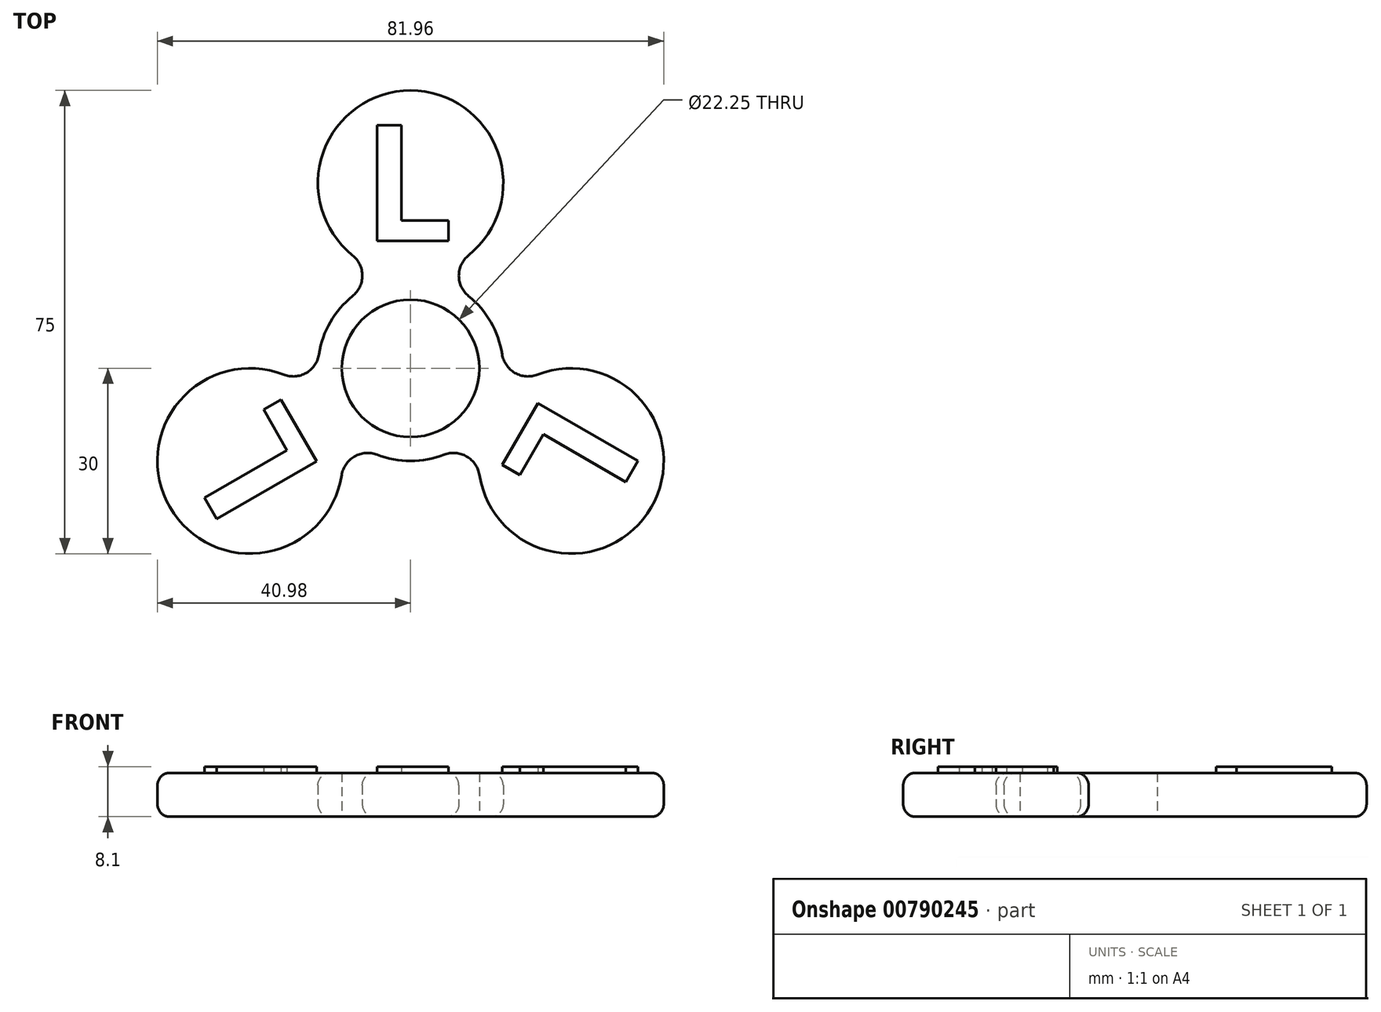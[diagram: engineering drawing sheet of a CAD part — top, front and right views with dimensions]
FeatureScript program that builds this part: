
annotation { "Feature Type Name" : "Feature", "Feature Type Description" : "" }
export const myFeature = defineFeature(function(context is Context, id is Id, definition is map)
    precondition{}
    {
        {
            var Q0;
            Q0=qCreatedBy(makeId("Top.planeOp"),FACE);
            var sketch = newSketch(context, id + "F0", { "sketchPlane" : qUnion([Q0])});
            skCircle(sketch, "E0", {"center": v(0, 0) * mm, "radius": 15 * mm});
            skCircle(sketch, "E1", {"center": v(0, 0) * mm, "radius": 11.12 * mm});
            skSolve(sketch);
        }
        {
            var Q0;
            Q0 = qSketchRegion(id + "F0", true);
            extrude(context, id + "F1", {"entities" : qUnion([Q0]), "depth" : 7.1 * mm, "offsetDistance" : 25 * mm});
        }
        {
            var Q0;
            Q0=qCreatedBy(makeId("Top.planeOp"),FACE);
            var sketch = newSketch(context, id + "F2", { "sketchPlane" : qUnion([Q0])});
            skArc(sketch, "E2", {"start": v(-9.4, 11.69) * mm, "mid": v(-7.81, 15) * mm, "end": v(-9.4, 18.31) * mm});
            skArc(sketch, "E3.MirrorCS", {"start": v(9.4, 11.69) * mm, "mid": v(7.81, 15) * mm, "end": v(9.4, 18.31) * mm});
            skArc(sketch, "E4", {"start": v(9.4, 18.31) * mm, "mid": v(0, 45) * mm, "end": v(-9.4, 18.31) * mm});
            skArc(sketch, "E5", {"start": v(9.4, 11.69) * mm, "mid": v(0, 15) * mm, "end": v(-9.4, 11.69) * mm});
            skArc(sketch, "E6.1.0", {"start": v(-5.42, -13.99) * mm, "mid": v(-9.08, -14.27) * mm, "end": v(-11.16, -17.3) * mm});
            skArc(sketch, "E6.1.1", {"start": v(-14.82, 2.3) * mm, "mid": v(-13, -7.5) * mm, "end": v(-5.42, -13.99) * mm});
            skArc(sketch, "E6.1.2", {"start": v(-14.82, 2.3) * mm, "mid": v(-16.9, -0.73) * mm, "end": v(-20.56, -1.01) * mm});
            skArc(sketch, "E6.1.3", {"start": v(-20.56, -1.01) * mm, "mid": v(-38.97, -22.5) * mm, "end": v(-11.16, -17.3) * mm});
            skArc(sketch, "E6.2.0", {"start": v(14.82, 2.3) * mm, "mid": v(16.9, -0.73) * mm, "end": v(20.56, -1.01) * mm});
            skArc(sketch, "E6.2.1", {"start": v(5.42, -13.99) * mm, "mid": v(13, -7.5) * mm, "end": v(14.82, 2.3) * mm});
            skArc(sketch, "E6.2.2", {"start": v(5.42, -13.99) * mm, "mid": v(9.08, -14.27) * mm, "end": v(11.16, -17.3) * mm});
            skArc(sketch, "E6.2.3", {"start": v(11.16, -17.3) * mm, "mid": v(38.97, -22.5) * mm, "end": v(20.56, -1.01) * mm});
            skSolve(sketch);
        }
        {
            var Q0;
            Q0 = qSketchRegion(id + "F2", true);
            extrude(context, id + "F3", {"entities" : qUnion([Q0]), "operationType" : NewBodyOperationType.ADD, "depth" : 7.1 * mm, "offsetDistance" : 25 * mm});
        }
        {
            var Q0;
            Q0=makeQuery(id+"F3.boolean.opBoolean","MERGE",FACE,{"derivedFrom":[makeQuery(id+"F1.opExtrude","CAP_FACE",FACE,{"disambiguationData":[OSD([sQuery(id+"F0.wireOp",EDGE,"E0"),sQuery(id+"F0.wireOp",EDGE,"E1")])],"isStart":false}),makeQuery(id+"F3.opExtrude","CAP_FACE",FACE,{"disambiguationData":[OSD([sQuery(id+"F2.wireOp",EDGE,"E2"),sQuery(id+"F2.wireOp",EDGE,"E3.MirrorCS"),sQuery(id+"F2.wireOp",EDGE,"E4"),sQuery(id+"F2.wireOp",EDGE,"E5")])],"isStart":false}),makeQuery(id+"F3.opExtrude","CAP_FACE",FACE,{"disambiguationData":[OSD([sQuery(id+"F2.wireOp",EDGE,"E6.1.0"),sQuery(id+"F2.wireOp",EDGE,"E6.1.1"),sQuery(id+"F2.wireOp",EDGE,"E6.1.2"),sQuery(id+"F2.wireOp",EDGE,"E6.1.3")])],"isStart":false}),makeQuery(id+"F3.opExtrude","CAP_FACE",FACE,{"disambiguationData":[OSD([sQuery(id+"F2.wireOp",EDGE,"E6.2.0"),sQuery(id+"F2.wireOp",EDGE,"E6.2.1"),sQuery(id+"F2.wireOp",EDGE,"E6.2.2"),sQuery(id+"F2.wireOp",EDGE,"E6.2.3")])],"isStart":false})]});
            var sketch = newSketch(context, id + "F4", { "sketchPlane" : qUnion([Q0])});
            skText(sketch, "E7", { "text": "L", "fontName": "OpenSans-Bold.ttf"});
            const initialGuessF4  = {"E7": [-0.0078, 0.02067, 1, 0, 0.01886]};
            skSetInitialGuess(sketch, initialGuessF4);
            skSolve(sketch);
        }
        {
            var Q0;
            Q0 = qSketchRegion(id + "F4", true);
            extrude(context, id + "F5", {"entities" : qUnion([Q0]), "depth" : 1 * mm, "offsetDistance" : 25 * mm});
        }
        {
            var Q0;
            Q0=qCreatedBy(makeId("Front.planeOp"),FACE);
            var sketch = newSketch(context, id + "F6", { "sketchPlane" : qUnion([Q0])});
            skLineSegment(sketch, "E8", {"start": v(0, 0) * mm, "end": v(0, 54.96) * mm});
            skSolve(sketch);
        }
        {
            var Q0;
            Q0=makeQuery(id+"F5.opExtrude","SWEPT_BODY",BODY,{"disambiguationData":[OSD([sQuery(id+"F4.wireOp",EDGE,"E7.sketch_text.stroke-0"),sQuery(id+"F4.wireOp",EDGE,"E7.sketch_text.stroke-1"),sQuery(id+"F4.wireOp",EDGE,"E7.sketch_text.stroke-2"),sQuery(id+"F4.wireOp",EDGE,"E7.sketch_text.stroke-3"),sQuery(id+"F4.wireOp",EDGE,"E7.sketch_text.stroke-4"),sQuery(id+"F4.wireOp",EDGE,"E7.sketch_text.stroke-5")])]});
            var Q1;
            Q1=sQuery(id+"F6.wireOp",EDGE,"E8");
            circularPattern(context, id + "F7", {"entities" : qUnion([Q0]), "axis" : qUnion([Q1]), "angle" : 360 * degree, "instanceCount" : 3, "equalSpace" : true});
        }
        {
            var Q0;
            Q0=makeQuery(id+"F3.opExtrude","CAP_EDGE",EDGE,{"disambiguationData":[OSD([sQuery(id+"F2.wireOp",EDGE,"E6.2.3")])],"isStart":false});
            fillet(context, id + "F8", {"entities" : qUnion([Q0]), "radius" : 2 * mm, "tangentPropagation" : true, "allowEdgeOverflow" : false});
        }
        {
            var Q0;
            Q0=makeQuery(id+"F3.opExtrude","CAP_EDGE",EDGE,{"disambiguationData":[OSD([sQuery(id+"F2.wireOp",EDGE,"E6.1.3")])],"isStart":true});
            fillet(context, id + "F9", {"entities" : qUnion([Q0]), "radius" : 2 * mm, "tangentPropagation" : true, "allowEdgeOverflow" : false});
        }
    });
